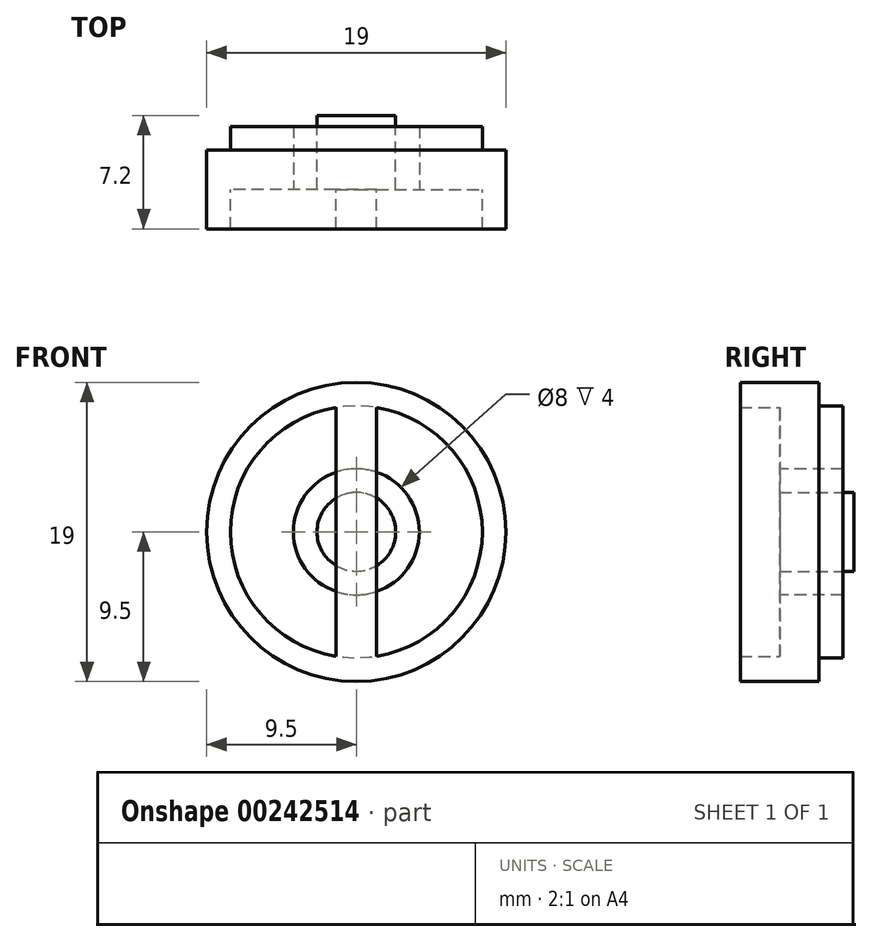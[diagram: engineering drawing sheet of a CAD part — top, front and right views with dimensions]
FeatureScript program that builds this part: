
annotation { "Feature Type Name" : "Feature", "Feature Type Description" : "" }
export const myFeature = defineFeature(function(context is Context, id is Id, definition is map)
    precondition{}
    {
        {
            var Q0;
            Q0=qCreatedBy(makeId("Front.planeOp"),FACE);
            var sketch = newSketch(context, id + "F0", { "sketchPlane" : qUnion([Q0])});
            skCircle(sketch, "E0", {"center": v(0, 0) * mm, "radius": 9.5 * mm});
            skCircle(sketch, "E1", {"center": v(0, 0) * mm, "radius": 8 * mm});
            skCircle(sketch, "E2", {"center": v(0, 0) * mm, "radius": 4 * mm});
            skSolve(sketch);
        }
        {
            var Q0;
            Q0=qSketchRegion(id+"F0",true);
            extrude(context, id + "F1", {"entities" : qUnion([Q0]), "depth" : 5 * mm, "symmetric" : true});
        }
        {
            var Q0;
            Q0=qCreatedBy(makeId("Front.planeOp"),FACE);
            var sketch = newSketch(context, id + "F2", { "sketchPlane" : qUnion([Q0])});
            skLineSegment(sketch, "E3.bottom", {"start": v(-1.3, 8.33) * mm, "end": v(1.3, 8.33) * mm});
            skLineSegment(sketch, "E3.top", {"start": v(-1.3, -8.33) * mm, "end": v(1.3, -8.33) * mm});
            skLineSegment(sketch, "E3.left", {"start": v(-1.3, 8.33) * mm, "end": v(-1.3, -8.33) * mm});
            skLineSegment(sketch, "E3.right", {"start": v(1.3, 8.33) * mm, "end": v(1.3, -8.33) * mm});
            skPoint(sketch, "E3.middle", {"position": v(0, 0) * mm});
            skSolve(sketch);
        }
        {
            var Q0;
            Q0=makeQuery(id+"F2.imprint","IMPRINT",FACE,{"disambiguationData":[TD([[makeQuery(id+"F2.imprint","IMPRINT",EDGE,{"derivedFrom":sQuery(id+"F2.wireOp",EDGE,"E3.bottom")}),-1.0]])]});
            var Q1;
            Q1=makeQuery(id+"F1.opExtrude","CAP_FACE",FACE,{"disambiguationData":[OSD([sQuery(id+"F0.wireOp",EDGE,"E0"),sQuery(id+"F0.wireOp",EDGE,"E1")])],"isStart":true});
            extrude(context, id + "F3", {"entities" : qUnion([Q0, Q1]), "operationType" : NewBodyOperationType.ADD, "depth" : 2.5 * mm});
        }
        {
            var Q0;
            Q0=makeQuery(id+"F0.imprint","IMPRINT",FACE,{"disambiguationData":[TD([[makeQuery(id+"F0.imprint","IMPRINT",EDGE,{"derivedFrom":sQuery(id+"F0.wireOp",EDGE,"E1")}),1.0]])]});
            extrude(context, id + "F4", {"entities" : qUnion([Q0]), "operationType" : NewBodyOperationType.ADD, "oppositeDirection" : true, "depth" : 4 * mm});
        }
        {
            var Q0;
            Q0=makeQuery(id+"F3.opExtrude","CAP_FACE",FACE,{"disambiguationData":[OSD([sQuery(id+"F2.wireOp",EDGE,"E3.bottom"),sQuery(id+"F2.wireOp",EDGE,"E3.top"),sQuery(id+"F2.wireOp",EDGE,"E3.left"),sQuery(id+"F2.wireOp",EDGE,"E3.right")])],"isStart":true});
            cPlane(context, id + "F5", {"entities" : qUnion([Q0]), "cplaneType" : CPlaneType.OFFSET, "offset" : 25 * mm, "width" : 150 * mm, "height" : 150 * mm});
        }
        {
            var Q0;
            Q0=qCreatedBy(id+"F5.planeOp",FACE);
            var sketch = newSketch(context, id + "F6", { "sketchPlane" : qUnion([Q0])});
            skCircle(sketch, "E4", {"center": v(0, 0) * mm, "radius": 2.5 * mm});
            skSolve(sketch);
        }
        {
            var Q0;
            Q0=makeQuery(id+"F6.imprint","IMPRINT",FACE,{"disambiguationData":[TD([[makeQuery(id+"F6.imprint","IMPRINT",EDGE,{"derivedFrom":sQuery(id+"F6.wireOp",EDGE,"E4")}),1.0]])]});
            extrude(context, id + "F7", {"entities" : qUnion([Q0]), "operationType" : NewBodyOperationType.ADD, "oppositeDirection" : true, "depth" : 25 * mm, "hasSecondDirection" : true, "secondDirectionOppositeDirection" : true, "secondDirectionDepth" : 20.3 * mm});
        }
    });
